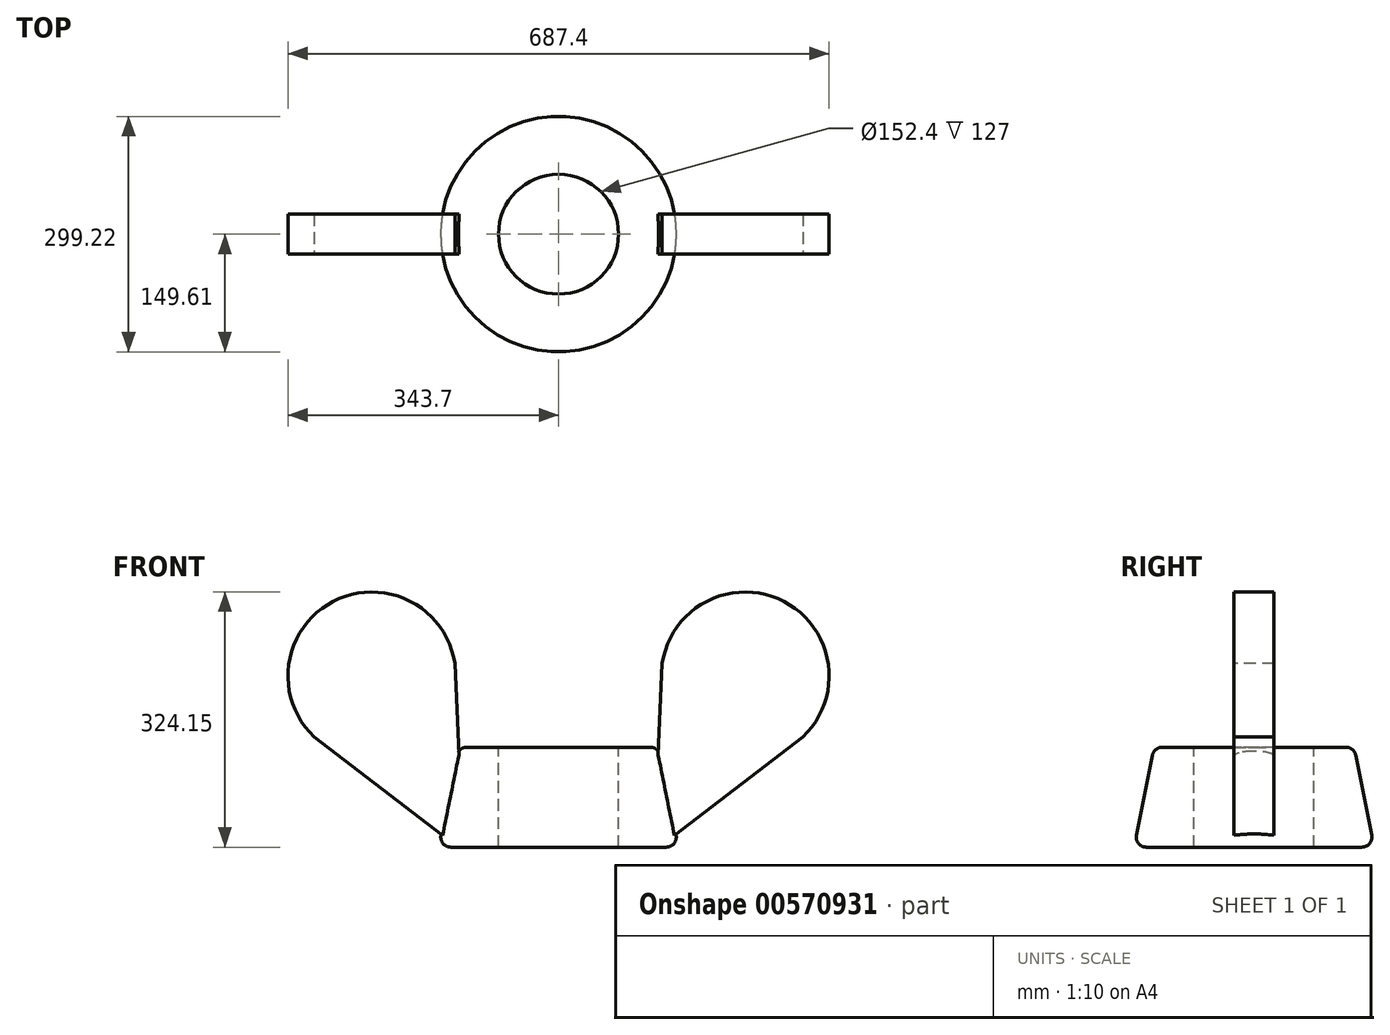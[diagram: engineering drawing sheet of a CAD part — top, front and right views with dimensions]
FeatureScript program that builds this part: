
annotation { "Feature Type Name" : "Feature", "Feature Type Description" : "" }
export const myFeature = defineFeature(function(context is Context, id is Id, definition is map)
    precondition{}
    {
        {
            var Q0;
            Q0=qCreatedBy(makeId("Top.planeOp"),FACE);
            var sketch = newSketch(context, id + "F0", { "sketchPlane" : qUnion([Q0])});
            skCircle(sketch, "E0", {"center": v(0, 0) * mm, "radius": 152.4 * mm});
            skSolve(sketch);
        }
        {
            var Q0;
            Q0=makeQuery(id+"F0.imprint","IMPRINT",FACE,{"disambiguationData":[TD([[makeQuery(id+"F0.imprint","IMPRINT",EDGE,{"derivedFrom":sQuery(id+"F0.wireOp",EDGE,"E0")}),1.0]])]});
            cPlane(context, id + "F1", {"entities" : qUnion([Q0]), "cplaneType" : CPlaneType.OFFSET, "offset" : 127 * mm, "width" : 152.4 * mm, "height" : 152.4 * mm});
        }
        {
            var Q0;
            Q0=qCreatedBy(id+"F1.planeOp",FACE);
            var sketch = newSketch(context, id + "F2", { "sketchPlane" : qUnion([Q0])});
            skCircle(sketch, "E1", {"center": v(0, 0) * mm, "radius": 127 * mm});
            skSolve(sketch);
        }
        {
            var Q0;
            Q0=makeQuery(id+"F2.imprint","IMPRINT",FACE,{"disambiguationData":[TD([[makeQuery(id+"F2.imprint","IMPRINT",EDGE,{"derivedFrom":sQuery(id+"F2.wireOp",EDGE,"E1")}),1.0]])]});
            var Q1;
            Q1=makeQuery(id+"F0.imprint","IMPRINT",FACE,{"disambiguationData":[TD([[makeQuery(id+"F0.imprint","IMPRINT",EDGE,{"derivedFrom":sQuery(id+"F0.wireOp",EDGE,"E0")}),1.0]])]});
            loft(context, id + "F3", {"sheetProfilesArray" : [{ "sheetProfileEntities" : qUnion([Q0]) }, { "sheetProfileEntities" : qUnion([Q1]) }]});
        }
        {
            var Q0;
            Q0=makeQuery(id+"F3.opLoft","MID_CAP_EDGE",EDGE,{"disambiguationData":[OSD([sQuery(id+"F2.wireOp",EDGE,"E1")])],"capPos":0.0});
            fillet(context, id + "F4", {"entities" : qUnion([Q0]), "radius" : 12.7 * mm, "tangentPropagation" : true, "allowEdgeOverflow" : false});
        }
        {
            var Q0;
            Q0=makeQuery(id+"F3.opLoft","MID_CAP_EDGE",EDGE,{"disambiguationData":[OSD([sQuery(id+"F0.wireOp",EDGE,"E0"),sQuery(id+"F2.wireOp",EDGE,"E1")])],"capPos":1.0});
            fillet(context, id + "F5", {"entities" : qUnion([Q0]), "radius" : 12.7 * mm, "tangentPropagation" : true, "allowEdgeOverflow" : false});
        }
        {
            var Q0;
            Q0=makeQuery(id+"F3.opLoft","CAP_FACE",FACE,{"disambiguationData":[OSD([makeQuery(id+"F2.imprint","IMPRINT",FACE,{"disambiguationData":[TD([[makeQuery(id+"F2.imprint","IMPRINT",EDGE,{"derivedFrom":sQuery(id+"F2.wireOp",EDGE,"E1")}),1.0]])]})])],"isStart":true});
            var sketch = newSketch(context, id + "F6", { "sketchPlane" : qUnion([Q0])});
            skCircle(sketch, "E2", {"center": v(0, 0) * mm, "radius": 76.2 * mm});
            skSolve(sketch);
        }
        {
            var Q0;
            Q0 = qSketchRegion(id + "F6", true);
            extrude(context, id + "F7", {"entities" : qUnion([Q0]), "operationType" : NewBodyOperationType.REMOVE, "endBound" : BoundingType.THROUGH_ALL, "oppositeDirection" : true, "depth" : 25.4 * mm, "offsetDistance" : 25.4 * mm});
        }
        {
            var Q0;
            Q0=makeQuery(id+"F3.opLoft","CAP_FACE",FACE,{"disambiguationData":[OSD([makeQuery(id+"F0.imprint","IMPRINT",FACE,{"disambiguationData":[TD([[makeQuery(id+"F0.imprint","IMPRINT",EDGE,{"derivedFrom":sQuery(id+"F0.wireOp",EDGE,"E0")}),1.0]])]})])],"isStart":true});
            cPlane(context, id + "F8", {"entities" : qUnion([Q0]), "cplaneType" : CPlaneType.OFFSET, "offset" : 15.24 * mm, "oppositeDirection" : true, "width" : 152.4 * mm, "height" : 152.4 * mm});
        }
        {
            var Q0;
            Q0=qCreatedBy(id+"F8.planeOp",FACE);
            var sketch = newSketch(context, id + "F9", { "sketchPlane" : qUnion([Q0])});
            skLineSegment(sketch, "E3.bottom", {"start": v(-147.19, -25.4) * mm, "end": v(-401.19, -25.4) * mm});
            skLineSegment(sketch, "E3.top", {"start": v(-147.19, 25.4) * mm, "end": v(-401.19, 25.4) * mm});
            skLineSegment(sketch, "E3.right", {"start": v(-401.19, -25.4) * mm, "end": v(-401.19, 25.4) * mm});
            skLineSegment(sketch, "E4", {"start": v(-147.19, -25.4) * mm, "end": v(-81.94, -25.4) * mm});
            skLineSegment(sketch, "E5", {"start": v(-81.94, -25.4) * mm, "end": v(-81.94, 25.4) * mm});
            skLineSegment(sketch, "E6", {"start": v(-147.19, 25.4) * mm, "end": v(-81.94, 25.4) * mm});
            skSolve(sketch);
        }
        {
            var Q0;
            Q0 = qSketchRegion(id + "F9", true);
            extrude(context, id + "F10", {"entities" : qUnion([Q0]), "operationType" : NewBodyOperationType.ADD, "oppositeDirection" : true, "depth" : 340.36 * mm, "offsetDistance" : 25.4 * mm});
        }
        {
            var Q0;
            Q0=makeQuery(id+"F10.opExtrude","SWEPT_FACE",FACE,{"disambiguationData":[OSD([sQuery(id+"F9.wireOp",EDGE,"E3.top"),sQuery(id+"F9.wireOp",EDGE,"E6")])]});
            var sketch = newSketch(context, id + "F11", { "sketchPlane" : qUnion([Q0])});
            skLineSegment(sketch, "E7", {"start": v(-126.52, 116.8) * mm, "end": v(-131.72, 233.25) * mm});
            skArc(sketch, "E8", {"start": v(-131.72, 233.25) * mm, "mid": v(-237.13, 324.15) * mm, "end": v(-342.54, 233.25) * mm});
            skArc(sketch, "E9", {"start": v(-342.54, 233.25) * mm, "mid": v(-337.84, 182.72) * mm, "end": v(-310.3, 140.1) * mm});
            skLineSegment(sketch, "E10", {"start": v(-195.89, -44.53) * mm, "end": v(-439.18, 15.24) * mm});
            skLineSegment(sketch, "E11", {"start": v(-439.18, 15.24) * mm, "end": v(-407.71, 94.96) * mm});
            skLineSegment(sketch, "E12", {"start": v(-407.71, 94.96) * mm, "end": v(-399.75, 461.04) * mm});
            skLineSegment(sketch, "E13", {"start": v(-399.75, 461.04) * mm, "end": v(-37.95, 528.22) * mm});
            skLineSegment(sketch, "E14", {"start": v(-37.95, 528.22) * mm, "end": v(-37.95, 195.96) * mm});
            skLineSegment(sketch, "E15", {"start": v(-37.95, 195.96) * mm, "end": v(-81.94, 127) * mm});
            skLineSegment(sketch, "E16", {"start": v(-81.94, 127) * mm, "end": v(-113.79, 127) * mm});
            skArc(sketch, "E17", {"start": v(-113.79, 127) * mm, "mid": v(-121.95, 124.13) * mm, "end": v(-126.52, 116.8) * mm});
            skLineSegment(sketch, "E18", {"start": v(-310.3, 140.1) * mm, "end": v(-147.18, 15.24) * mm});
            skLineSegment(sketch, "E19", {"start": v(-147.18, 15.24) * mm, "end": v(-126.52, 116.8) * mm});
            skLineSegment(sketch, "E20", {"start": v(-195.89, -44.53) * mm, "end": v(-147.18, 15.24) * mm});
            skSolve(sketch);
        }
        {
            var Q0;
            {var subQ3=sQuery(id+"F11.wireOp",EDGE,"E10");Q0=makeQuery(id+"F11.imprint","IMPRINT",FACE,{"disambiguationData":[TD([[makeQuery(id+"F11.imprint","IMPRINT",EDGE,{"derivedFrom":subQ3}),-1.0]])]});}
            var Q1;
            Q1=makeQuery(id+"F11.imprint","IMPRINT",FACE,{"disambiguationData":[TD([[makeQuery(id+"F11.imprint","IMPRINT",EDGE,{"derivedFrom":sQuery(id+"F11.wireOp",EDGE,"E7")}),-1.0]])]});
            extrude(context, id + "F12", {"entities" : qUnion([Q0, Q1]), "operationType" : NewBodyOperationType.REMOVE, "endBound" : BoundingType.THROUGH_ALL, "oppositeDirection" : true, "depth" : 25.4 * mm, "offsetDistance" : 25.4 * mm});
        }
        {
            var Q0;
            Q0=makeQuery(id+"F3.opLoft","SWEPT_BODY",BODY,{"disambiguationData":[OSD([makeQuery(id+"F0.imprint","IMPRINT",FACE,{"disambiguationData":[TD([[makeQuery(id+"F0.imprint","IMPRINT",EDGE,{"derivedFrom":sQuery(id+"F0.wireOp",EDGE,"E0")}),1.0]])]}),makeQuery(id+"F2.imprint","IMPRINT",FACE,{"disambiguationData":[TD([[makeQuery(id+"F2.imprint","IMPRINT",EDGE,{"derivedFrom":sQuery(id+"F2.wireOp",EDGE,"E1")}),1.0]])]})])]});
            var Q1;
            Q1=qCreatedBy(makeId("Right.planeOp"),FACE);
            mirror(context, id + "F13", {"operationType" : NewBodyOperationType.ADD, "entities" : qUnion([Q0]), "mirrorPlane" : qUnion([Q1])});
        }
    });
